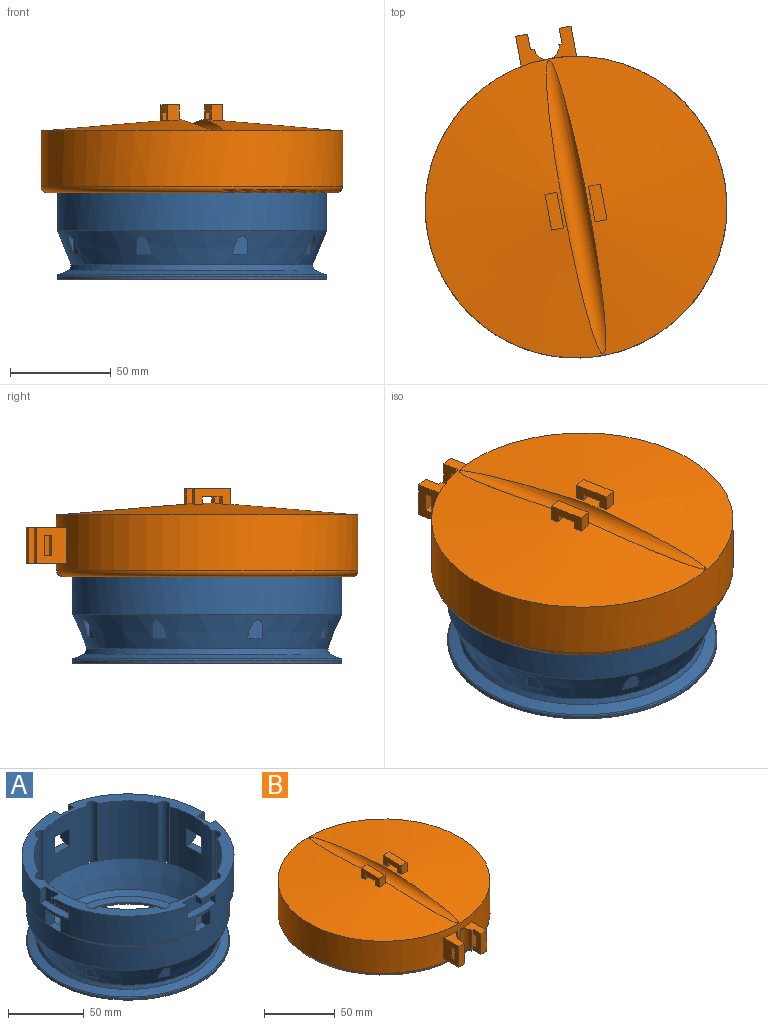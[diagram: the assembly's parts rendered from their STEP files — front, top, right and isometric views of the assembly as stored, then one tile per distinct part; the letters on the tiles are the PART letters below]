
ASSEMBLY  parts=2 mates=1
PART A: 89 faces, bbox 145x145x70 mm
  f0: cylinder r=62mm len=46.34mm, axis (0,0,-1), area 1689.1mm2, adj f10,f17,f70,f76,f85,f86,f87,f88
  f1: cylinder r=62mm len=46.34mm, axis (0,0,-1), area 1689.1mm2, adj f10,f17,f66,f68,f81,f82,f83,f84
  f2: cylinder r=70mm len=140mm, axis (0,0,1), area 8973mm2, adj f3,f4,f10,f23,f24,f25,f28,f29
  f3: cone r=70mm half-angle=45deg, axis (0,0,1), area 397mm2, adj f2,f12,f28,f86
  f4: cone r=70mm half-angle=45deg, axis (0,0,1), area 397mm2, adj f2,f12,f30,f83
  f5: cylinder r=62mm len=46.34mm, axis (0,0,-1), area 1689.1mm2, adj f10,f17,f23,f24,f25,f26,f78,f80
  f6: cylinder r=62mm len=46.34mm, axis (0,0,-1), area 1885.5mm2, adj f10,f17,f76,f78
  f7: cylinder r=62mm len=46.34mm, axis (0,0,-1), area 1689.1mm2, adj f10,f17,f27,f28,f29,f30,f72,f74
  f8: cylinder r=62mm len=46.34mm, axis (0,0,-1), area 1885.5mm2, adj f10,f17,f68,f72
  f9: cylinder r=62mm len=46.34mm, axis (0,0,-1), area 1885.5mm2, adj f10,f17,f70,f74
  f10: plane 140x140mm, normal (0,0,1), area 2846.7mm2, adj f0,f1,f2,f5,f6,f7,f8,f9
  f11: cylinder r=62mm len=46.34mm, axis (0,0,-1), area 1885.5mm2, adj f10,f17,f66,f80
  f12: cylinder r=67mm len=134mm, axis (0,0,1), area 7971.1mm2, adj f3,f4,f13,f26,f27,f63,f64,f82
  f13: cone r=59.18mm half-angle=22.6deg, axis (0,0,1), area 6797.6mm2, adj f12,f21,f65,f66,f67,f68,f69,f70
  f14: cone r=67mm half-angle=67.4deg, axis (0,0,-1), area 2377.2mm2, adj f21,f22
  f15: cylinder r=67mm len=134mm, axis (0,0,1), area 617.2mm2, adj f16,f22
  f16: plane 134x134mm, normal (0,0,-1), area 8293.8mm2, adj f15,f20
  f17: cone r=62mm half-angle=23.3deg, axis (0,0,1), area 7640.5mm2, adj f0,f1,f5,f6,f7,f8,f9,f11
  f18: cone r=53.69mm half-angle=56.6deg, axis (0,0,1), area 1624.7mm2, adj f17,f19
  f19: plane 99x99mm, normal (0,0,1), area 1888.9mm2, adj f18,f20
  f20: cylinder r=43mm len=86mm, axis (0,0,-1), area 432.3mm2, adj f16,f19
  f21: cone r=59.95mm half-angle=22.4deg, axis (0,0,-1), area 1075mm2, adj f13,f14
  f22: torus R=66.2mm, axis (0,0,-1), area 395.4mm2, adj f14,f15
  f23: plane 14.01x8.05mm, normal (1,0,0), area 108.1mm2, adj f2,f5,f24,f26,f64
  f24: plane 14x8.4mm, normal (0,0,-1), area 112.2mm2, adj f2,f5,f23,f25
  f25: plane 14.01x8.05mm, normal (-1,0,0), area 108.1mm2, adj f2,f5,f24,f26,f63
  f26: plane 14x5.4mm, normal (0,0,1), area 70.1mm2, adj f5,f12,f23,f25
  f27: plane 14x5.4mm, normal (0,0,1), area 70.1mm2, adj f7,f12,f28,f30
  f28: plane 14.01x8.05mm, normal (-1,0,0), area 108.1mm2, adj f2,f3,f7,f27,f29
  f29: plane 14x8.4mm, normal (0,0,-1), area 112.2mm2, adj f2,f7,f28,f30
  f30: plane 14.01x8.05mm, normal (1,0,0), area 108.1mm2, adj f2,f4,f7,f27,f29
  f31: plane 5.99x2mm, normal (-1,0,0), area 12mm2, adj f2,f32,f37,f38
  f32: plane 12x5.99mm, normal (0,0,-1), area 66.7mm2, adj f2,f31,f33,f38
  f33: plane 8x4.78mm, normal (1,0,0), area 38.3mm2, adj f2,f32,f34,f38
  f34: plane 26x6mm, normal (0,0,1), area 145.5mm2, adj f2,f33,f35,f38
  f35: plane 11x4.78mm, normal (-1,0,0), area 52.6mm2, adj f2,f10,f34,f38
  f36: plane 5.99x5mm, normal (1,0,0), area 30mm2, adj f2,f10,f37,f38
  f37: plane 6x2mm, normal (0,0,-1), area 12mm2, adj f2,f31,f36,f38
  f38: plane 26x11mm, normal (0,1,0), area 240mm2, adj f10,f31,f32,f33,f34,f35,f36,f37
  f39: plane 5.99x5mm, normal (0,-1,0), area 30mm2, adj f2,f10,f45,f46
  f40: plane 11x4.78mm, normal (0,1,0), area 52.6mm2, adj f2,f10,f41,f46
  f41: plane 26x6mm, normal (0,0,1), area 145.5mm2, adj f2,f40,f42,f46
  f42: plane 8x4.78mm, normal (0,-1,0), area 38.3mm2, adj f2,f41,f43,f46
  f43: plane 12x5.99mm, normal (0,0,-1), area 66.7mm2, adj f2,f42,f44,f46
  f44: plane 5.99x2mm, normal (0,1,0), area 12mm2, adj f2,f43,f45,f46
  f45: plane 6x2mm, normal (0,0,-1), area 12mm2, adj f2,f39,f44,f46
  f46: plane 26x11mm, normal (1,0,0), area 240mm2, adj f10,f39,f40,f41,f42,f43,f44,f45
  f47: plane 5.99x5mm, normal (-1,0,0), area 30mm2, adj f2,f10,f53,f54
  f48: plane 11x4.78mm, normal (1,0,0), area 52.6mm2, adj f2,f10,f49,f54
  f49: plane 26x6mm, normal (0,0,1), area 145.5mm2, adj f2,f48,f50,f54
  f50: plane 8x4.78mm, normal (-1,0,0), area 38.3mm2, adj f2,f49,f51,f54
  f51: plane 12x5.99mm, normal (0,0,-1), area 66.7mm2, adj f2,f50,f52,f54
  f52: plane 5.99x2mm, normal (1,0,0), area 12mm2, adj f2,f51,f53,f54
  f53: plane 6x2mm, normal (0,0,-1), area 12mm2, adj f2,f47,f52,f54
  f54: plane 26x11mm, normal (0,-1,0), area 240mm2, adj f10,f47,f48,f49,f50,f51,f52,f53
  f55: plane 5.99x2mm, normal (0,-1,0), area 12mm2, adj f2,f56,f61,f62
  f56: plane 12x5.99mm, normal (0,0,-1), area 66.7mm2, adj f2,f55,f57,f62
  f57: plane 8x4.78mm, normal (0,1,0), area 38.3mm2, adj f2,f56,f58,f62
  f58: plane 26x6mm, normal (0,0,1), area 145.5mm2, adj f2,f57,f59,f62
  f59: plane 11x4.78mm, normal (0,-1,0), area 52.6mm2, adj f2,f10,f58,f62
  f60: plane 5.99x5mm, normal (0,1,0), area 30mm2, adj f2,f10,f61,f62
  f61: plane 6x2mm, normal (0,0,-1), area 12mm2, adj f2,f55,f60,f62
  f62: plane 26x11mm, normal (-1,0,0), area 240mm2, adj f10,f55,f56,f57,f58,f59,f60,f61
  f63: cone r=70mm half-angle=45deg, axis (0,0,1), area 397mm2, adj f2,f12,f25,f88
  f64: cone r=70mm half-angle=45deg, axis (0,0,1), area 397mm2, adj f2,f12,f23,f81
  f65: cylinder r=62mm len=11.63mm, axis (0,0,1), area 93.1mm2, adj f13,f17,f66
  f66: cylinder r=4mm len=57.97mm, axis (0,0,1), area 664.5mm2, adj f1,f10,f11,f13,f65
  f67: cylinder r=62mm len=11.63mm, axis (0,0,1), area 93.1mm2, adj f13,f17,f68
  f68: cylinder r=4mm len=57.97mm, axis (0,0,1), area 664.5mm2, adj f1,f8,f10,f13,f67
  f69: cylinder r=62mm len=11.63mm, axis (0,0,1), area 93.1mm2, adj f13,f17,f70
  f70: cylinder r=4mm len=57.97mm, axis (0,0,1), area 664.5mm2, adj f0,f9,f10,f13,f69
  f71: cylinder r=62mm len=11.63mm, axis (0,0,1), area 93.1mm2, adj f13,f17,f72
  f72: cylinder r=4mm len=57.97mm, axis (0,0,1), area 664.5mm2, adj f7,f8,f10,f13,f71
  f73: cylinder r=62mm len=11.63mm, axis (0,0,1), area 93.1mm2, adj f13,f17,f74
  f74: cylinder r=4mm len=57.97mm, axis (0,0,1), area 664.5mm2, adj f7,f9,f10,f13,f73
  f75: cylinder r=62mm len=11.63mm, axis (0,0,1), area 93.1mm2, adj f13,f17,f76
  f76: cylinder r=4mm len=57.97mm, axis (0,0,1), area 664.5mm2, adj f0,f6,f10,f13,f75
  f77: cylinder r=62mm len=11.63mm, axis (0,0,1), area 93.1mm2, adj f13,f17,f78
  f78: cylinder r=4mm len=57.97mm, axis (0,0,1), area 664.5mm2, adj f5,f6,f10,f13,f77
  f79: cylinder r=62mm len=11.63mm, axis (0,0,1), area 93.1mm2, adj f13,f17,f80
  f80: cylinder r=4mm len=57.97mm, axis (0,0,1), area 664.5mm2, adj f5,f10,f11,f13,f79
  f81: plane 14.01x8.05mm, normal (0,-1,0), area 108.1mm2, adj f1,f2,f64,f82,f84
  f82: plane 14x5.4mm, normal (0,0,1), area 70.1mm2, adj f1,f12,f81,f83
  f83: plane 14.01x8.05mm, normal (0,1,0), area 108.1mm2, adj f1,f2,f4,f82,f84
  f84: plane 14x8.4mm, normal (0,0,-1), area 112.2mm2, adj f1,f2,f81,f83
  f85: plane 14x8.4mm, normal (0,0,-1), area 112.2mm2, adj f0,f2,f86,f88
  f86: plane 14.01x8.05mm, normal (0,1,0), area 108.1mm2, adj f0,f2,f3,f85,f87
  f87: plane 14x5.4mm, normal (0,0,1), area 70.1mm2, adj f0,f12,f86,f88
  f88: plane 14.01x8.05mm, normal (0,-1,0), area 108.1mm2, adj f0,f2,f63,f85,f87
PART B: 67 faces, bbox 163x170.8x44.3 mm
  f0: plane 18x15.32mm, normal (-1,0,0), area 236.4mm2, adj f4,f51,f52,f53,f58,f64,f65,f66
  f1: plane 18x15.32mm, normal (1,0,0), area 236.4mm2, adj f4,f54,f55,f56,f60,f61,f62,f63
  f2: plane 18x7.93mm, normal (1,0,0), area 103.4mm2, adj f51,f52,f53,f58,f64,f65,f66
  f3: plane 18x7.93mm, normal (-1,0,0), area 103.4mm2, adj f54,f55,f56,f60,f61,f62,f63
  f4: cylinder r=75mm len=150mm, axis (0,0,1), area 12586.7mm2, adj f0,f1,f5,f9,f51,f52,f54,f55
  f5: cone r=0mm half-angle=85.2deg, axis (0,0,-1), area 15083.1mm2, adj f4,f30,f31,f32,f33,f35,f36,f37
  f6: cylinder r=71mm len=142mm, axis (0,0,1), area 11876mm2, adj f7,f8,f10,f11,f12,f13,f15,f16
  f7: plane 144x144mm, normal (0,0,-1), area 449.2mm2, adj f6,f9
  f8: plane 142x142mm, normal (0,0,-1), area 15836.8mm2, adj f6
  f9: torus R=72mm, axis (0,0,-1), area 2188.4mm2, adj f4,f7
  f10: plane 9.46x4.01mm, normal (0,0.03,1), area 36.9mm2, adj f6,f12,f13,f14
  f11: plane 9.46x4.01mm, normal (0,0.03,-1), area 36.9mm2, adj f6,f12,f13,f14
  f12: plane 4.46x3.84mm, normal (-1,0.03,0), area 16.7mm2, adj f6,f10,f11,f14
  f13: plane 4.46x3.84mm, normal (1,0.03,0), area 16.7mm2, adj f6,f10,f11,f14
  f14: plane 9.21x4.22mm, normal (0,1,0), area 38.9mm2, adj f10,f11,f12,f13
  f15: plane 9.46x4.01mm, normal (0,-0.03,1), area 36.9mm2, adj f6,f17,f18,f19
  f16: plane 9.46x4.01mm, normal (0,-0.03,-1), area 36.9mm2, adj f6,f17,f18,f19
  f17: plane 4.46x3.84mm, normal (-1,-0.03,0), area 16.7mm2, adj f6,f15,f16,f19
  f18: plane 4.46x3.84mm, normal (1,-0.03,0), area 16.7mm2, adj f6,f15,f16,f19
  f19: plane 9.21x4.22mm, normal (0,-1,0), area 38.9mm2, adj f15,f16,f17,f18
  f20: plane 9.46x4mm, normal (-0.03,0,1), area 36.9mm2, adj f6,f22,f23,f24
  f21: plane 9.46x4mm, normal (-0.03,0,-1), area 36.9mm2, adj f6,f22,f23,f24
  f22: plane 4.46x3.84mm, normal (-0.03,-1,0), area 16.7mm2, adj f6,f20,f21,f24
  f23: plane 4.46x3.84mm, normal (-0.03,1,0), area 16.7mm2, adj f6,f20,f21,f24
  f24: plane 9.21x4.22mm, normal (-1,0,0), area 38.9mm2, adj f20,f21,f22,f23
  f25: plane 9.46x4.01mm, normal (0.03,0,1), area 36.9mm2, adj f6,f27,f28,f29
  f26: plane 9.46x4.01mm, normal (0.03,0,-1), area 36.9mm2, adj f6,f27,f28,f29
  f27: plane 4.46x3.84mm, normal (0.03,-1,0), area 16.7mm2, adj f6,f25,f26,f29
  f28: plane 4.46x3.84mm, normal (0.03,1,0), area 16.7mm2, adj f6,f25,f26,f29
  f29: plane 9.21x4.22mm, normal (1,0,0), area 38.9mm2, adj f25,f26,f27,f28
  f30: cylinder r=6.25mm len=148.32mm, axis (0,-1,0), area 1872.8mm2, adj f5
  f31: plane 8.47x6.47mm, normal (0,-1,0), area 47.2mm2, adj f5,f32,f38,f39,f40
  f32: plane 1.91x1.14mm, normal (0,0,-1), area 1mm2, adj f5,f31,f39
  f33: plane 6.6x4.53mm, normal (0,1,0), area 22.2mm2, adj f5,f34,f39,f40
  f34: plane 10x6mm, normal (0,0,-1), area 60mm2, adj f33,f35,f39,f40
  f35: plane 6.6x4.53mm, normal (0,-1,0), area 22.2mm2, adj f5,f34,f39,f40
  f36: plane 1.91x1.14mm, normal (0,0,-1), area 1mm2, adj f5,f37,f39
  f37: plane 8.47x6.47mm, normal (0,1,0), area 47.2mm2, adj f5,f36,f38,f39,f40
  f38: plane 18x6mm, normal (0,0,1), area 108mm2, adj f31,f37,f39,f40
  f39: plane 18.08x8.08mm, normal (1,0,0), area 103.8mm2, adj f5,f31,f32,f33,f34,f35,f36,f37
  f40: plane 18.43x8.12mm, normal (-1,0,0), area 100.6mm2, adj f5,f31,f33,f34,f35,f37,f38
  f41: plane 8.47x6.47mm, normal (0,-1,0), area 47.2mm2, adj f5,f42,f48,f49,f50
  f42: plane 1.91x1.14mm, normal (0,0,-1), area 1mm2, adj f5,f41,f49
  f43: plane 6.6x4.53mm, normal (0,1,0), area 22.2mm2, adj f5,f44,f49,f50
  f44: plane 10x6mm, normal (0,0,-1), area 60mm2, adj f43,f45,f49,f50
  f45: plane 6.6x4.53mm, normal (0,-1,0), area 22.2mm2, adj f5,f44,f49,f50
  f46: plane 1.91x1.14mm, normal (0,0,-1), area 1mm2, adj f5,f47,f49
  f47: plane 8.47x6.47mm, normal (0,1,0), area 47.2mm2, adj f5,f46,f48,f49,f50
  f48: plane 18x6mm, normal (0,0,1), area 108mm2, adj f41,f47,f49,f50
  f49: plane 18.08x8.08mm, normal (-1,0,0), area 103.8mm2, adj f5,f41,f42,f43,f44,f45,f46,f47
  f50: plane 18.43x8.12mm, normal (1,0,0), area 100.6mm2, adj f5,f41,f43,f44,f45,f47,f48
  f51: plane 15.32x12.43mm, normal (0,0,1), area 107.2mm2, adj f0,f2,f4,f53,f57,f58
  f52: plane 15.32x12.43mm, normal (0,0,-1), area 107.2mm2, adj f0,f2,f4,f53,f57,f58
  f53: plane 18x6mm, normal (0,-1,0), area 108mm2, adj f0,f2,f51,f52
  f54: plane 15.32x12.73mm, normal (0,0,1), area 109.2mm2, adj f1,f3,f4,f56,f59,f60
  f55: plane 15.32x12.73mm, normal (0,0,-1), area 109.2mm2, adj f1,f3,f4,f56,f59,f60
  f56: plane 18x6mm, normal (0,-1,0), area 108mm2, adj f1,f3,f54,f55
  f57: cylinder r=6.25mm len=18mm, axis (0,0,1), area 151.1mm2, adj f4,f51,f52,f58
  f58: plane 18x7.59mm, normal (0,-1,0), area 88.6mm2, adj f0,f2,f51,f52,f57,f65,f66
  f59: cylinder r=6.25mm len=18mm, axis (0,0,1), area 150.6mm2, adj f4,f54,f55,f60
  f60: plane 18x7.91mm, normal (0,-1,0), area 94.4mm2, adj f1,f3,f54,f55,f59,f61,f63
  f61: plane 6x3.93mm, normal (0,0,1), area 23.6mm2, adj f1,f3,f60,f62
  f62: plane 10x6mm, normal (0,1,0), area 60mm2, adj f1,f3,f61,f63
  f63: plane 6x3.93mm, normal (0,0,-1), area 23.6mm2, adj f1,f3,f60,f62
  f64: plane 10x6mm, normal (0,1,0), area 60mm2, adj f0,f2,f65,f66
  f65: plane 6x3.93mm, normal (0,0,-1), area 23.6mm2, adj f0,f2,f58,f64
  f66: plane 6x3.93mm, normal (0,0,1), area 23.6mm2, adj f0,f2,f58,f64
PLACE A t=(-39.72,-6.6,-6.78)mm fixed
PLACE B rot(axis=(0,0,-1),169.5deg) t=(-39.72,-6.6,96.9)mm
MATE revolute B.f4 <-> A.f0  axis (0,0,-1) through (-39.72,-6.6,63.22)mm
